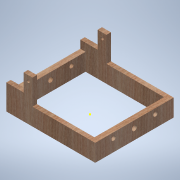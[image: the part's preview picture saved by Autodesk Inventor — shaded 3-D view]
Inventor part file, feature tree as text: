
AUTODESK INVENTOR PART (.ipt)
format: ipt  version: 2021.3 (Build 253353000, 353)  size: 200,192 bytes
history: native  units: mm
features: sketch x7, extrude x6, plane x5, reference x5
ambient origin geometry x8: Origin, YZ Plane, XZ Plane, XY Plane, X Axis, Y Axis, Z Axis, Center Point
bodies: Solid1 (feature_tree)
feature tree (23):
  extrude  "Extrusion1"  Depth=266.0mm
  extrude  "Extrusion2"  Depth=17.0mm
  extrude  "Extrusion3"  Depth=20.0mm
  plane  "Work Plane1"
  plane  "Work Plane2"
  plane  "Work Plane3"
  sketch  "Sketch9"  dims[d6=66.0mm d7=0.0mm d8=30.0mm d9=0.0mm]
  plane  "Work Plane4"
  extrude  "Extrusion8"  Depth=30.0mm TaperAngle=0.0deg
  sketch  "Sketch10"  dims[d14=100.0mm d15=17.0mm]
  plane  "Work Plane5"
  extrude  "Extrusion9"  Depth=17.0mm
  extrude  "Extrusion10"  Depth=17.0mm
  sketch  "Sketch12"  dims[d20=30.0mm d21=0.0mm d33=30.0mm d34=0.0mm d35=30.0mm d36=0.0mm d37=30.0mm d38=0.0mm]
  sketch  "Sketch1"  dims[d0=300.0mm d1=266.0mm]
  sketch  "Sketch2"  dims[d2=17.0mm d3=17.0mm]
  reference  "Reference1"
  reference  "Reference2"
  sketch  "Sketch4"  dims[d4=20.0mm d5=20.0mm]
  reference  "Reference3"
  reference  "Reference7"
  reference  "Reference8"
  sketch  "Sketch11"  dims[d17=100.0mm d18=17.0mm]
